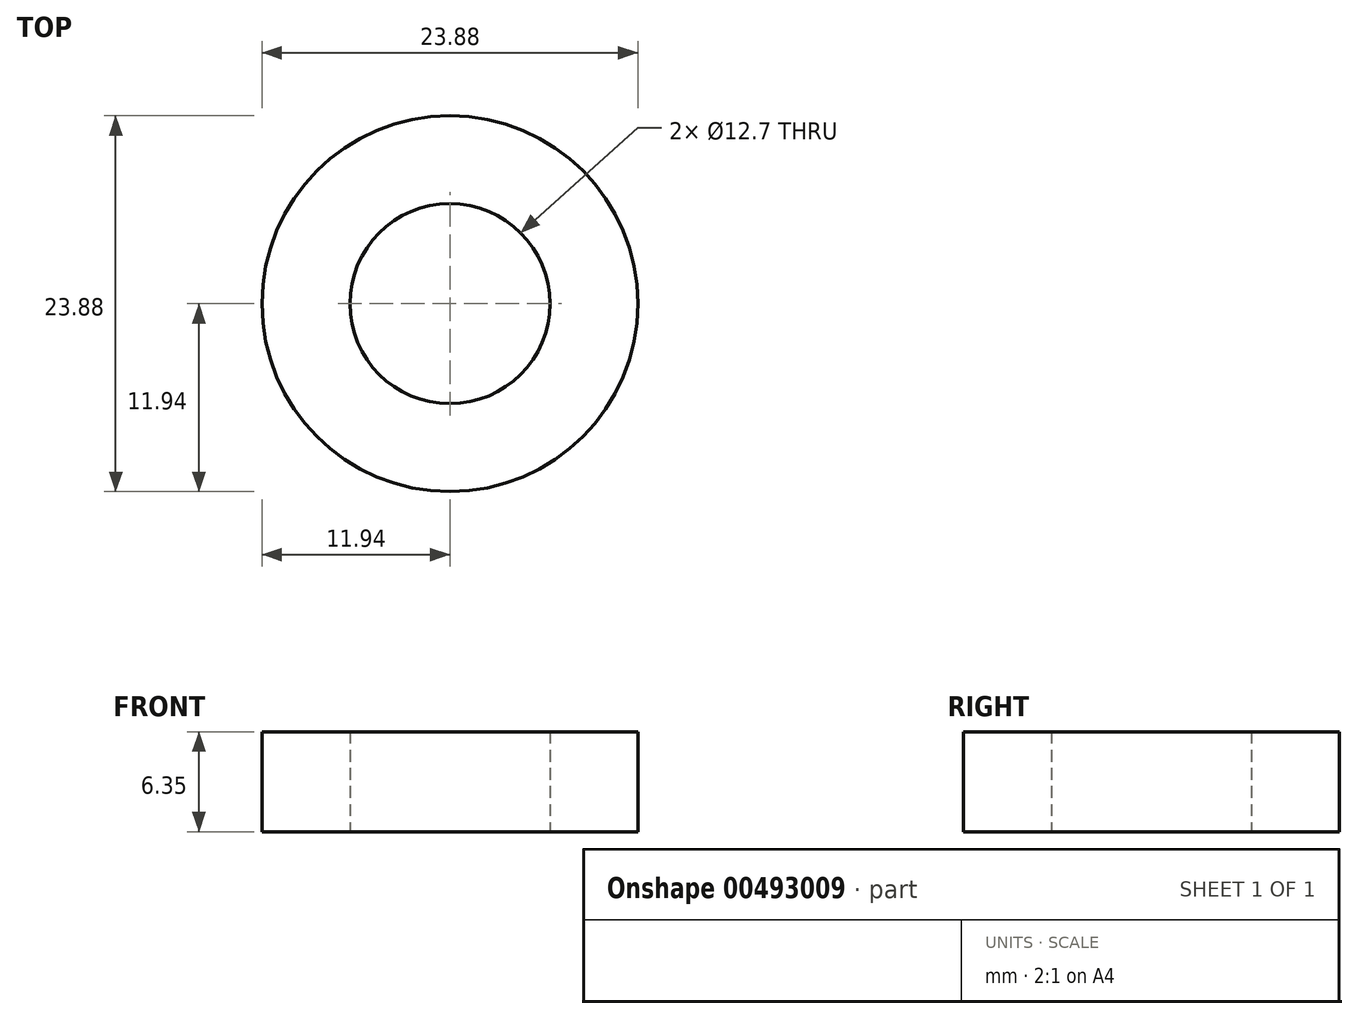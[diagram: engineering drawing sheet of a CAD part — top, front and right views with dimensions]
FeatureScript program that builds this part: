
annotation { "Feature Type Name" : "Feature", "Feature Type Description" : "" }
export const myFeature = defineFeature(function(context is Context, id is Id, definition is map)
    precondition{}
    {
        {
            var Q0;
            Q0=qCreatedBy(makeId("Top.planeOp"),FACE);
            var sketch = newSketch(context, id + "F0", { "sketchPlane" : qUnion([Q0])});
            skCircle(sketch, "E0", {"center": v(0, 0) * mm, "radius": 11.94 * mm});
            skCircle(sketch, "E1", {"center": v(0, 0) * mm, "radius": 6.35 * mm});
            skSolve(sketch);
        }
        {
            var Q0;
            Q0 = qSketchRegion(id + "F0", true);
            extrude(context, id + "F1", {"entities" : qUnion([Q0]), "depth" : 6.35 * mm, "offsetDistance" : 25.4 * mm});
        }
    });
